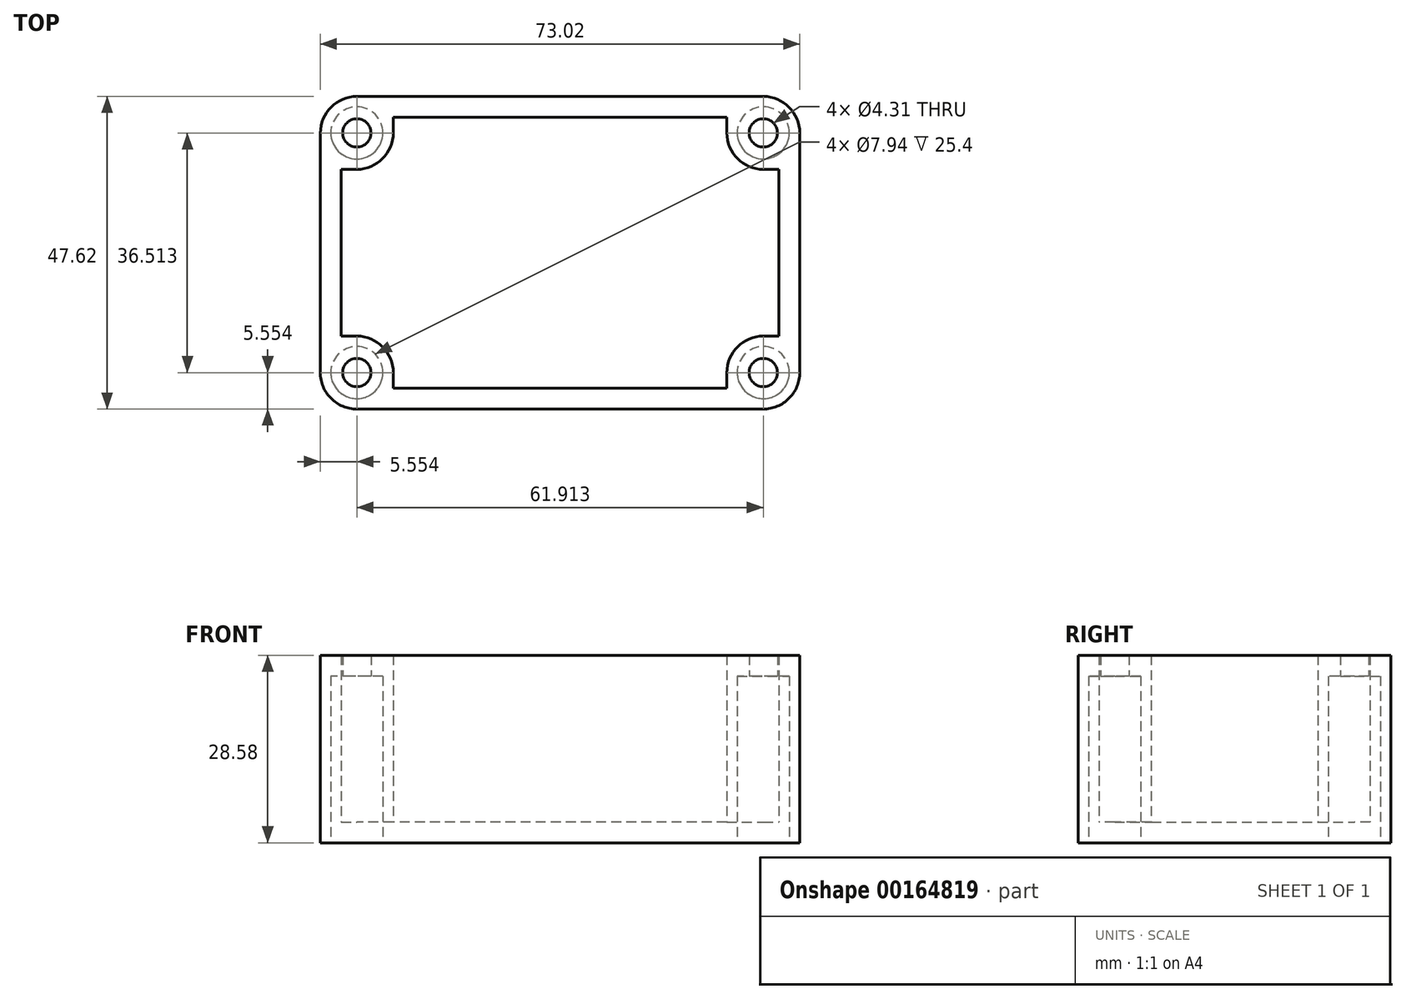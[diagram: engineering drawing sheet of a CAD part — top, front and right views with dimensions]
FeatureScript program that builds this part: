
annotation { "Feature Type Name" : "Feature", "Feature Type Description" : "" }
export const myFeature = defineFeature(function(context is Context, id is Id, definition is map)
    precondition{}
    {
        {
            var Q0;
            Q0=qCreatedBy(makeId("Top.planeOp"),FACE);
            var sketch = newSketch(context, id + "F0", { "sketchPlane" : qUnion([Q0])});
            skLineSegment(sketch, "E0.bottom", {"start": v(0, 0) * mm, "end": v(7.94, 0) * mm});
            skLineSegment(sketch, "E0.left", {"start": v(0, 0) * mm, "end": v(0, -7.94) * mm});
            skLineSegment(sketch, "E1.bottom", {"start": v(0, -7.94) * mm, "end": v(-50.8, -7.94) * mm});
            skLineSegment(sketch, "E1.top", {"start": v(11.11, -11.11) * mm, "end": v(-61.91, -11.11) * mm});
            skLineSegment(sketch, "E2.left", {"start": v(7.94, 0) * mm, "end": v(7.94, 25.4) * mm});
            skLineSegment(sketch, "E2.right", {"start": v(11.11, -11.11) * mm, "end": v(11.11, 36.51) * mm});
            skLineSegment(sketch, "E3.bottom", {"start": v(7.94, 25.4) * mm, "end": v(0, 25.4) * mm});
            skLineSegment(sketch, "E3.right", {"start": v(0, 25.4) * mm, "end": v(0, 33.34) * mm});
            skLineSegment(sketch, "E4.bottom", {"start": v(0, 33.34) * mm, "end": v(-50.8, 33.34) * mm});
            skLineSegment(sketch, "E4.top", {"start": v(11.11, 36.51) * mm, "end": v(-61.91, 36.51) * mm});
            skLineSegment(sketch, "E5.top", {"start": v(-50.8, 25.4) * mm, "end": v(-58.74, 25.4) * mm});
            skLineSegment(sketch, "E5.left", {"start": v(-50.8, 33.34) * mm, "end": v(-50.8, 25.4) * mm});
            skLineSegment(sketch, "E6.left", {"start": v(-58.74, 25.4) * mm, "end": v(-58.74, 0) * mm});
            skLineSegment(sketch, "E6.right", {"start": v(-61.91, 36.51) * mm, "end": v(-61.91, -11.11) * mm});
            skLineSegment(sketch, "E7.bottom", {"start": v(-58.74, 0) * mm, "end": v(-50.8, 0) * mm});
            skLineSegment(sketch, "E7.right", {"start": v(-50.8, 0) * mm, "end": v(-50.8, -7.94) * mm});
            skLineSegment(sketch, "E8", {"start": v(-25.4, -7.94) * mm, "end": v(-25.4, -11.11) * mm, "construction": true});
            skLineSegment(sketch, "E9", {"start": v(-58.74, 12.7) * mm, "end": v(-61.91, 12.7) * mm, "construction": true});
            skLineSegment(sketch, "E10", {"start": v(-25.4, 33.34) * mm, "end": v(-25.4, 36.51) * mm, "construction": true});
            skLineSegment(sketch, "E11", {"start": v(7.94, 12.7) * mm, "end": v(11.11, 12.7) * mm, "construction": true});
            skLineSegment(sketch, "E12", {"start": v(-25.4, -7.94) * mm, "end": v(-25.4, 33.34) * mm, "construction": true});
            skCircle(sketch, "E13", {"center": v(-56.36, -5.56) * mm, "radius": 5.56 * mm, "construction": true});
            skLineSegment(sketch, "E14.bottom", {"start": v(-56.36, -5.56) * mm, "end": v(5.56, -5.56) * mm, "construction": true});
            skLineSegment(sketch, "E14.top", {"start": v(-56.36, 30.96) * mm, "end": v(5.56, 30.96) * mm, "construction": true});
            skLineSegment(sketch, "E14.left", {"start": v(-56.36, -5.56) * mm, "end": v(-56.36, 30.96) * mm, "construction": true});
            skLineSegment(sketch, "E14.right", {"start": v(5.56, -5.56) * mm, "end": v(5.56, 30.96) * mm, "construction": true});
            skPoint(sketch, "E14.middle", {"position": v(-25.4, 12.7) * mm});
            skCircle(sketch, "E15", {"center": v(5.56, -5.56) * mm, "radius": 2.15 * mm});
            skCircle(sketch, "E16", {"center": v(-56.36, -5.56) * mm, "radius": 2.15 * mm});
            skCircle(sketch, "E17", {"center": v(-56.36, 30.96) * mm, "radius": 2.15 * mm});
            skCircle(sketch, "E18", {"center": v(5.56, 30.96) * mm, "radius": 2.15 * mm});
            skSolve(sketch);
        }
        {
            var Q0;
            Q0 = qSketchRegion(id + "F0", true);
            extrude(context, id + "F1", {"entities" : qUnion([Q0]), "depth" : 25.4 * mm});
        }
        {
            var Q0;
            Q0=makeQuery(id+"F1.opExtrude","CAP_FACE",FACE,{"disambiguationData":[OSD([sQuery(id+"F0.wireOp",EDGE,"E0.bottom"),sQuery(id+"F0.wireOp",EDGE,"E0.left"),sQuery(id+"F0.wireOp",EDGE,"E1.bottom"),sQuery(id+"F0.wireOp",EDGE,"E1.top"),sQuery(id+"F0.wireOp",EDGE,"E2.left"),sQuery(id+"F0.wireOp",EDGE,"E2.right"),sQuery(id+"F0.wireOp",EDGE,"E3.bottom"),sQuery(id+"F0.wireOp",EDGE,"E3.right"),sQuery(id+"F0.wireOp",EDGE,"E4.bottom"),sQuery(id+"F0.wireOp",EDGE,"E4.top"),sQuery(id+"F0.wireOp",EDGE,"E5.top"),sQuery(id+"F0.wireOp",EDGE,"E5.left"),sQuery(id+"F0.wireOp",EDGE,"E6.left"),sQuery(id+"F0.wireOp",EDGE,"E6.right"),sQuery(id+"F0.wireOp",EDGE,"E7.bottom"),sQuery(id+"F0.wireOp",EDGE,"E7.right"),sQuery(id+"F0.wireOp",EDGE,"E15"),sQuery(id+"F0.wireOp",EDGE,"E16"),sQuery(id+"F0.wireOp",EDGE,"E17"),sQuery(id+"F0.wireOp",EDGE,"E18")])],"isStart":true});
            var sketch = newSketch(context, id + "F2", { "sketchPlane" : qUnion([Q0])});
            skCircle(sketch, "E19", {"center": v(5.56, 5.56) * mm, "radius": 2.15 * mm});
            skCircle(sketch, "E20", {"center": v(5.56, -30.96) * mm, "radius": 2.15 * mm});
            skCircle(sketch, "E21", {"center": v(-56.36, -30.96) * mm, "radius": 2.15 * mm});
            skCircle(sketch, "E22", {"center": v(-56.36, 5.56) * mm, "radius": 2.15 * mm});
            skLineSegment(sketch, "E23.bottom", {"start": v(11.11, -36.51) * mm, "end": v(-61.91, -36.51) * mm});
            skLineSegment(sketch, "E23.top", {"start": v(11.11, 11.11) * mm, "end": v(-61.91, 11.11) * mm});
            skLineSegment(sketch, "E23.left", {"start": v(11.11, -36.51) * mm, "end": v(11.11, 11.11) * mm});
            skLineSegment(sketch, "E23.right", {"start": v(-61.91, -36.51) * mm, "end": v(-61.91, 11.11) * mm});
            skSolve(sketch);
        }
        {
            var Q0;
            Q0 = qSketchRegion(id + "F2", true);
            extrude(context, id + "F3", {"entities" : qUnion([Q0]), "operationType" : NewBodyOperationType.ADD, "depth" : 3.17 * mm});
        }
        {
            var Q0;
            Q0=makeQuery(id+"F1.opExtrude","SWEPT_EDGE",EDGE,{"disambiguationData":[OSD([sQuery(id+"F0.wireOp",EDGE,"E5.top"),sQuery(id+"F0.wireOp",EDGE,"E5.left")])]});
            var Q1;
            Q1=makeQuery(id+"F3.boolean.opBoolean","MERGE",EDGE,{"derivedFrom":[makeQuery(id+"F1.opExtrude","SWEPT_EDGE",EDGE,{"disambiguationData":[OSD([sQuery(id+"F0.wireOp",EDGE,"E4.top"),sQuery(id+"F0.wireOp",EDGE,"E6.right")])]}),makeQuery(id+"F3.opExtrude","SWEPT_EDGE",EDGE,{"disambiguationData":[OSD([sQuery(id+"F2.wireOp",EDGE,"E23.bottom"),sQuery(id+"F2.wireOp",EDGE,"E23.right")])]})]});
            var Q2;
            Q2=makeQuery(id+"F1.opExtrude","SWEPT_EDGE",EDGE,{"disambiguationData":[OSD([sQuery(id+"F0.wireOp",EDGE,"E3.bottom"),sQuery(id+"F0.wireOp",EDGE,"E3.right")])]});
            var Q3;
            Q3=makeQuery(id+"F3.boolean.opBoolean","MERGE",EDGE,{"derivedFrom":[makeQuery(id+"F1.opExtrude","SWEPT_EDGE",EDGE,{"disambiguationData":[OSD([sQuery(id+"F0.wireOp",EDGE,"E2.right"),sQuery(id+"F0.wireOp",EDGE,"E4.top")])]}),makeQuery(id+"F3.opExtrude","SWEPT_EDGE",EDGE,{"disambiguationData":[OSD([sQuery(id+"F2.wireOp",EDGE,"E23.bottom"),sQuery(id+"F2.wireOp",EDGE,"E23.left")])]})]});
            var Q4;
            Q4=makeQuery(id+"F1.opExtrude","SWEPT_EDGE",EDGE,{"disambiguationData":[OSD([sQuery(id+"F0.wireOp",EDGE,"E0.bottom"),sQuery(id+"F0.wireOp",EDGE,"E0.left")])]});
            var Q5;
            Q5=makeQuery(id+"F3.boolean.opBoolean","MERGE",EDGE,{"derivedFrom":[makeQuery(id+"F1.opExtrude","SWEPT_EDGE",EDGE,{"disambiguationData":[OSD([sQuery(id+"F0.wireOp",EDGE,"E1.top"),sQuery(id+"F0.wireOp",EDGE,"E2.right")])]}),makeQuery(id+"F3.opExtrude","SWEPT_EDGE",EDGE,{"disambiguationData":[OSD([sQuery(id+"F2.wireOp",EDGE,"E23.top"),sQuery(id+"F2.wireOp",EDGE,"E23.left")])]})]});
            var Q6;
            Q6=makeQuery(id+"F1.opExtrude","SWEPT_EDGE",EDGE,{"disambiguationData":[OSD([sQuery(id+"F0.wireOp",EDGE,"E7.bottom"),sQuery(id+"F0.wireOp",EDGE,"E7.right")])]});
            var Q7;
            Q7=makeQuery(id+"F3.boolean.opBoolean","MERGE",EDGE,{"derivedFrom":[makeQuery(id+"F1.opExtrude","SWEPT_EDGE",EDGE,{"disambiguationData":[OSD([sQuery(id+"F0.wireOp",EDGE,"E1.top"),sQuery(id+"F0.wireOp",EDGE,"E6.right")])]}),makeQuery(id+"F3.opExtrude","SWEPT_EDGE",EDGE,{"disambiguationData":[OSD([sQuery(id+"F2.wireOp",EDGE,"E23.top"),sQuery(id+"F2.wireOp",EDGE,"E23.right")])]})]});
            fillet(context, id + "F4", {"entities" : qUnion([Q0, Q1, Q2, Q3, Q4, Q5, Q6, Q7]), "radius" : 5.56 * mm, "tangentPropagation" : true, "allowEdgeOverflow" : false});
        }
        {
            var Q0;
            Q0=makeQuery(id+"F3.opExtrude","CAP_FACE",FACE,{"disambiguationData":[OSD([sQuery(id+"F2.wireOp",EDGE,"E19"),sQuery(id+"F2.wireOp",EDGE,"E20"),sQuery(id+"F2.wireOp",EDGE,"E21"),sQuery(id+"F2.wireOp",EDGE,"E22"),sQuery(id+"F2.wireOp",EDGE,"E23.bottom"),sQuery(id+"F2.wireOp",EDGE,"E23.top"),sQuery(id+"F2.wireOp",EDGE,"E23.left"),sQuery(id+"F2.wireOp",EDGE,"E23.right")])],"isStart":false});
            var sketch = newSketch(context, id + "F5", { "sketchPlane" : qUnion([Q0])});
            skCircle(sketch, "E24", {"center": v(-56.36, 5.56) * mm, "radius": 3.97 * mm});
            skCircle(sketch, "E25", {"center": v(5.56, 5.56) * mm, "radius": 3.97 * mm});
            skCircle(sketch, "E26", {"center": v(5.56, -30.96) * mm, "radius": 3.97 * mm});
            skCircle(sketch, "E27", {"center": v(-56.36, -30.96) * mm, "radius": 3.97 * mm});
            skSolve(sketch);
        }
        {
            var Q0;
            Q0=makeQuery(id+"F1.opExtrude","CAP_FACE",FACE,{"disambiguationData":[OSD([sQuery(id+"F0.wireOp",EDGE,"E0.bottom"),sQuery(id+"F0.wireOp",EDGE,"E0.left"),sQuery(id+"F0.wireOp",EDGE,"E1.bottom"),sQuery(id+"F0.wireOp",EDGE,"E1.top"),sQuery(id+"F0.wireOp",EDGE,"E2.left"),sQuery(id+"F0.wireOp",EDGE,"E2.right"),sQuery(id+"F0.wireOp",EDGE,"E3.bottom"),sQuery(id+"F0.wireOp",EDGE,"E3.right"),sQuery(id+"F0.wireOp",EDGE,"E4.bottom"),sQuery(id+"F0.wireOp",EDGE,"E4.top"),sQuery(id+"F0.wireOp",EDGE,"E5.top"),sQuery(id+"F0.wireOp",EDGE,"E5.left"),sQuery(id+"F0.wireOp",EDGE,"E6.left"),sQuery(id+"F0.wireOp",EDGE,"E6.right"),sQuery(id+"F0.wireOp",EDGE,"E7.bottom"),sQuery(id+"F0.wireOp",EDGE,"E7.right"),sQuery(id+"F0.wireOp",EDGE,"E15"),sQuery(id+"F0.wireOp",EDGE,"E16"),sQuery(id+"F0.wireOp",EDGE,"E17"),sQuery(id+"F0.wireOp",EDGE,"E18")])],"isStart":false});
            cPlane(context, id + "F6", {"entities" : qUnion([Q0]), "cplaneType" : CPlaneType.OFFSET, "offset" : 3.17 * mm, "oppositeDirection" : true, "width" : 152.4 * mm, "height" : 152.4 * mm});
        }
        {
            var Q0;
            Q0 = qSketchRegion(id + "F5", true);
            var Q1;
            Q1=qCreatedBy(id+"F6.planeOp",FACE);
            extrude(context, id + "F7", {"entities" : qUnion([Q0]), "operationType" : NewBodyOperationType.REMOVE, "endBound" : BoundingType.UP_TO_SURFACE, "oppositeDirection" : true, "endBoundEntityFace" : qUnion([Q1]), "depth" : 6.35 * mm});
        }
    });
